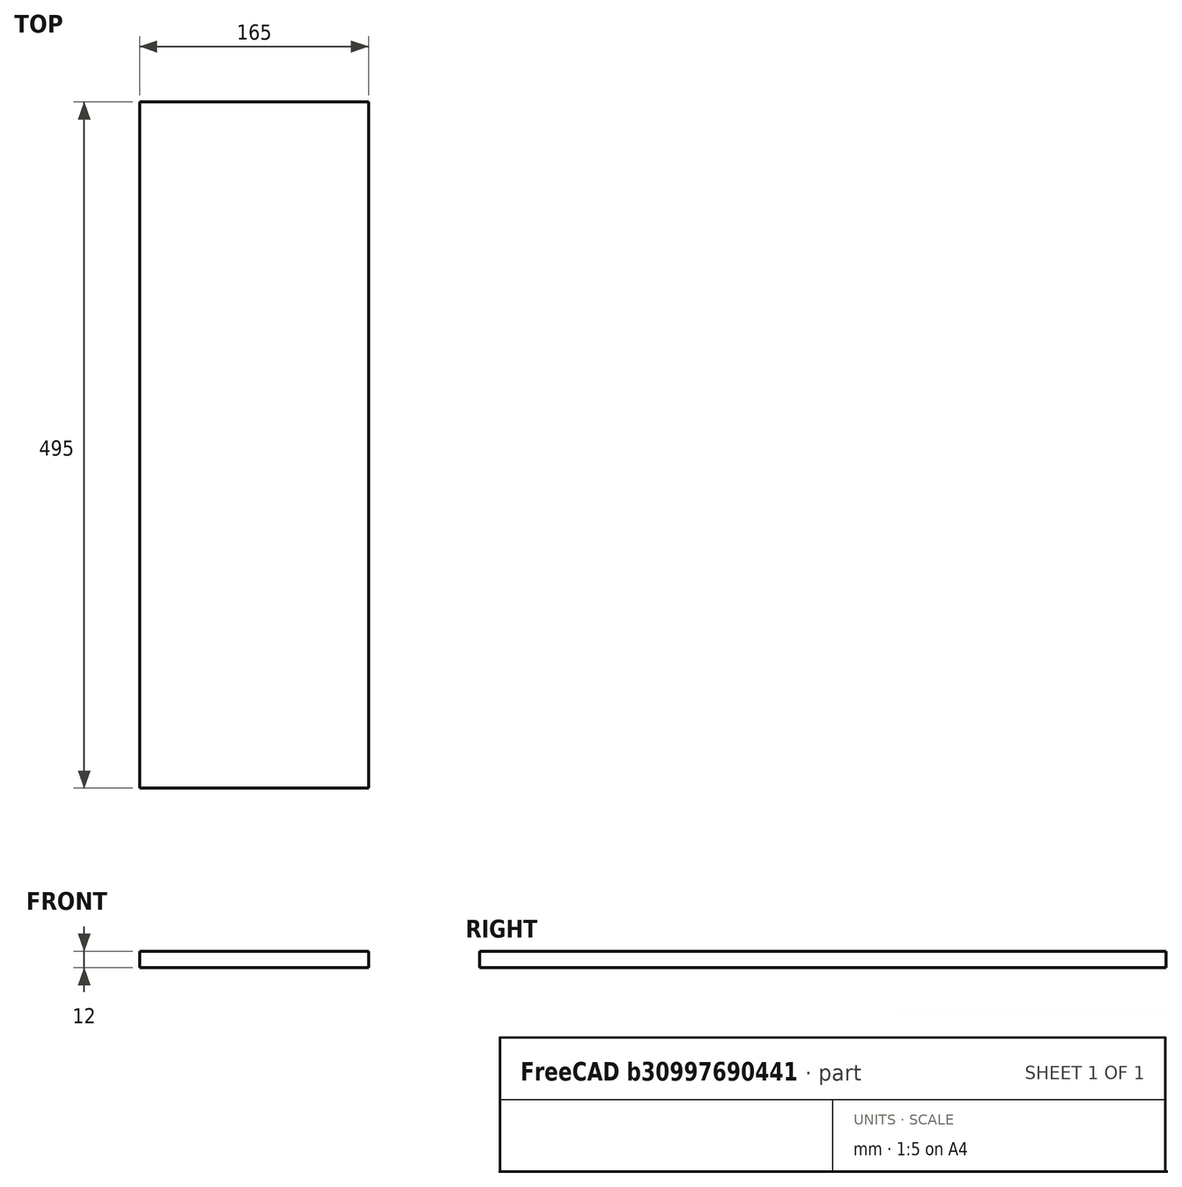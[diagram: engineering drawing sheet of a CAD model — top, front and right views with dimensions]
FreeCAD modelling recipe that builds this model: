
FCSTD DOCUMENT  (FreeCAD 0.20R29177 (Git))
Label: 1001_keyboard_500_16_Duo_LASER
License: All rights reserved
LicenseURL: http://en.wikipedia.org/wiki/All_rights_reserved
objects: Sketcher::SketchObject×1, PartDesign::Pad×1, PartDesign::Body×1, Spreadsheet::Sheet×1
note: 4 computed .brp shape members not serialized (recipe doc carries the construction recipe); baked Part::Feature solids carry a one-line shape summary decoded from their .brp

FEATURE [Sketcher::SketchObject] Sketch
  FullyConstrained = true
  MapMode = 5
  Support = -> [XY_Plane]
  expr: Constraints[5] = <<xls>>.k_w
  expr: Constraints[6] = <<xls>>.k_d
  sketch-geometry (5):
    g0: LineSegment StartX=0 StartY=495 StartZ=0 EndX=165 EndY=495 EndZ=0
    g1: LineSegment StartX=165 StartY=495 StartZ=0 EndX=165 EndY=0 EndZ=0
    g2: LineSegment StartX=165 StartY=0 StartZ=0 EndX=0 EndY=0 EndZ=0
    g3: LineSegment StartX=0 StartY=0 StartZ=0 EndX=0 EndY=247.5 EndZ=0
    g4: LineSegment StartX=0 StartY=247.5 StartZ=0 EndX=0 EndY=495 EndZ=0
  constraints (14):
    c: Coincident(g0,g1)
    c: Coincident(g1,g2)
    c: Horizontal(g0)
    c: Horizontal(g2)
    c: Vertical(g1)
    c: DistanceY(g1,g1) = 495
    c: DistanceX(g0,g0) = 165
    c: Coincident(g3,g2)
    c: Coincident(g4,g0)
    c: Equal(g3,g4)
    c: Vertical(g4)
    c: Vertical(g3)
    c: Coincident(g3,g4)
    c: Coincident(g2,g-1)
FEATURE [PartDesign::Pad] Pad
  AllowMultiFace = false
  Direction = (0,0,1)
  Length = 12
  Length2 = 100
  Profile = -> Sketch
  Type = 0
  expr: Length = <<xls>>.k_t_0
FEATURE [PartDesign::Body] Body
  Group = -> [Sketch,Pad]
  Origin = -> Origin
  Tip = -> Pad
FEATURE [Spreadsheet::Sheet] Spreadsheet  label="xls"
  cells = B3=KEABOPARD; B4=Thickness; C4=k_t_0; D4(k_t_0)=12; E4=mm; F4=Note:; G4=Plexi is 3mm; B5=Width; C5=k_w; D5(k_w)=495; E5=mm; B6=Deapth; C6=k_d; D6(k_d)=165; E6=mm; B9=Hole to Front Edge; B10=ToEdge; C10=hole_to_edge; D10(hole_to_edge)=80; E10=mm
